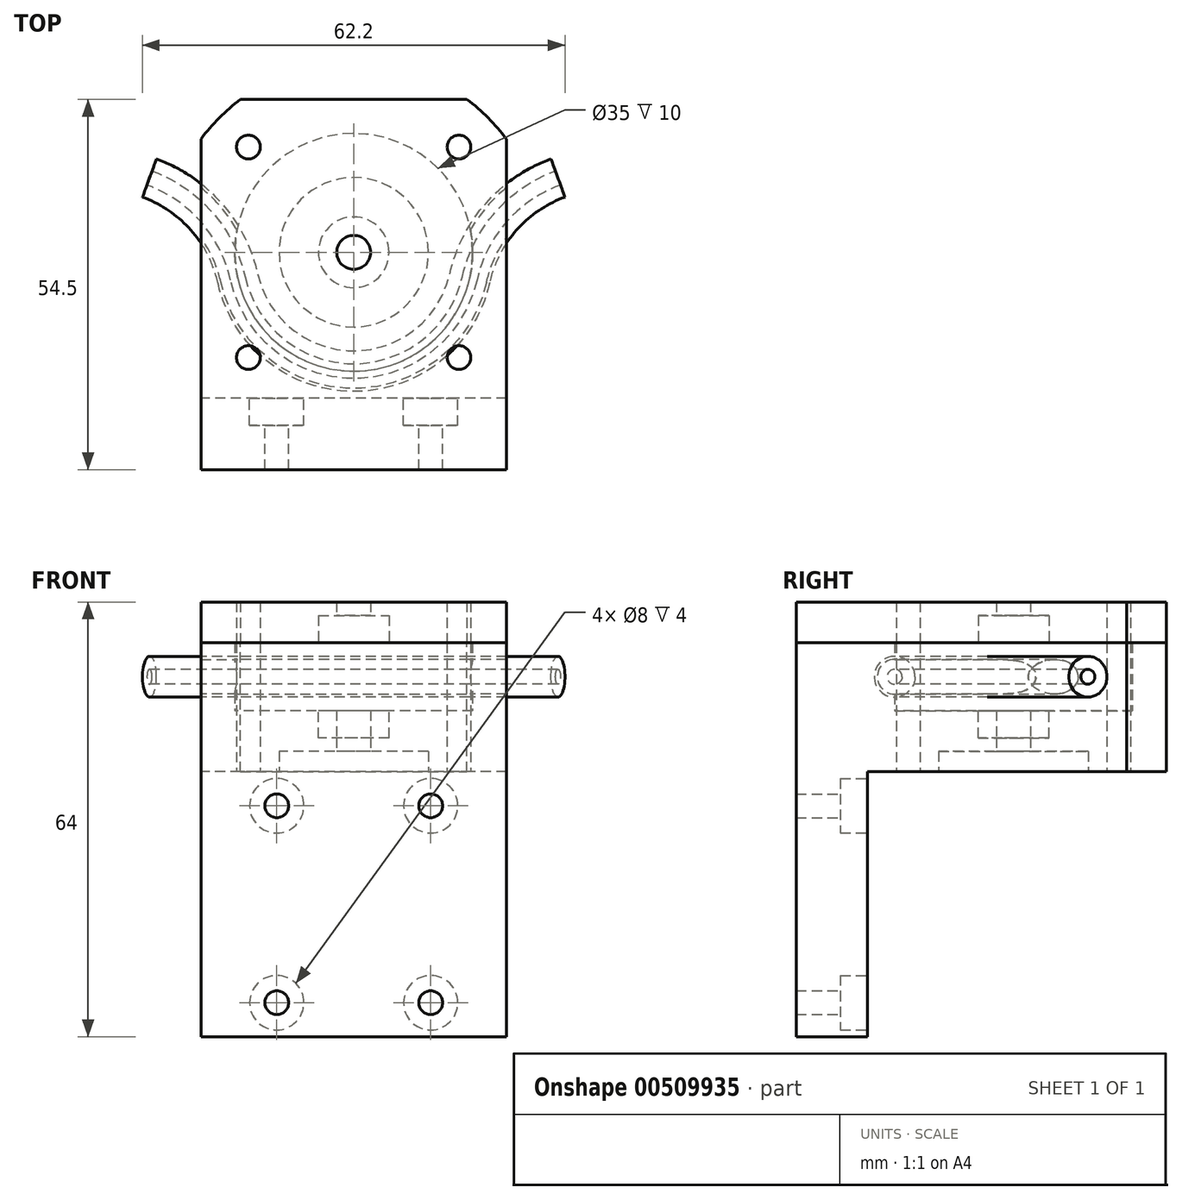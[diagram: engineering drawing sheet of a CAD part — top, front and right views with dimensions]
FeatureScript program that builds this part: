
annotation { "Feature Type Name" : "Feature", "Feature Type Description" : "" }
export const myFeature = defineFeature(function(context is Context, id is Id, definition is map)
    precondition{}
    {
        {
            var Q0;
            Q0=qCreatedBy(makeId("Top.planeOp"),FACE);
            var sketch = newSketch(context, id + "F0", { "sketchPlane" : qUnion([Q0])});
            skLineSegment(sketch, "E0", {"start": v(-21.5, -16.33) * mm, "end": v(-21.5, 16.33) * mm});
            skLineSegment(sketch, "E1", {"start": v(-16.33, 21.5) * mm, "end": v(16.33, 21.5) * mm});
            skLineSegment(sketch, "E2", {"start": v(21.5, 16.33) * mm, "end": v(21.5, -16.33) * mm});
            skLineSegment(sketch, "E3", {"start": v(16.33, -21.5) * mm, "end": v(-16.33, -21.5) * mm});
            skArc(sketch, "E4", {"start": v(-16.33, 21.5) * mm, "mid": v(-19.1, 19.1) * mm, "end": v(-21.5, 16.33) * mm});
            skArc(sketch, "E5", {"start": v(21.5, 16.33) * mm, "mid": v(19.1, 19.1) * mm, "end": v(16.33, 21.5) * mm});
            skCircle(sketch, "E6", {"center": v(-15.5, 15.5) * mm, "radius": 1.75 * mm});
            skCircle(sketch, "E7", {"center": v(15.5, 15.5) * mm, "radius": 1.75 * mm});
            skCircle(sketch, "E8", {"center": v(0, 0) * mm, "radius": 11 * mm});
            skCircle(sketch, "E9", {"center": v(-15.5, -15.5) * mm, "radius": 1.75 * mm});
            skCircle(sketch, "E10", {"center": v(15.5, -15.5) * mm, "radius": 1.75 * mm});
            skArc(sketch, "E11", {"start": v(-21.5, -16.33) * mm, "mid": v(-19.1, -19.1) * mm, "end": v(-16.33, -21.5) * mm});
            skArc(sketch, "E12", {"start": v(16.33, -21.5) * mm, "mid": v(19.1, -19.1) * mm, "end": v(21.5, -16.33) * mm});
            skLineSegment(sketch, "E13.bottom", {"start": v(15.5, 15.5) * mm, "end": v(-15.5, 15.5) * mm, "construction": true});
            skLineSegment(sketch, "E13.top", {"start": v(15.5, -15.5) * mm, "end": v(-15.5, -15.5) * mm, "construction": true});
            skLineSegment(sketch, "E13.left", {"start": v(15.5, 15.5) * mm, "end": v(15.5, -15.5) * mm, "construction": true});
            skLineSegment(sketch, "E13.right", {"start": v(-15.5, 15.5) * mm, "end": v(-15.5, -15.5) * mm, "construction": true});
            skLineSegment(sketch, "E14", {"start": v(0, 21.5) * mm, "end": v(0, -21.5) * mm, "construction": true});
            skLineSegment(sketch, "E15", {"start": v(-21.5, 0) * mm, "end": v(21.5, 0) * mm, "construction": true});
            skPoint(sketch, "E15.endSnap0", {"position": v(21.5, 0) * mm});
            skCircle(sketch, "E16", {"center": v(0, 0) * mm, "radius": 2.5 * mm});
            skSolve(sketch);
        }
        {
            var Q0;
            Q0=makeQuery(id+"F0.imprint","IMPRINT",FACE,{"disambiguationData":[TD([[makeQuery(id+"F0.imprint","IMPRINT",EDGE,{"derivedFrom":sQuery(id+"F0.wireOp",EDGE,"E0")}),-1.0]])]});
            var Q1;
            Q1=makeQuery(id+"F0.imprint","IMPRINT",FACE,{"disambiguationData":[TD([[makeQuery(id+"F0.imprint","IMPRINT",EDGE,{"derivedFrom":sQuery(id+"F0.wireOp",EDGE,"E8")}),1.0]])]});
            extrude(context, id + "F1", {"entities" : qUnion([Q0, Q1]), "depth" : 2 * mm, "offsetDistance" : 25 * mm});
        }
        {
            var Q0;
            Q0=makeQuery(id+"F1.opExtrude","CAP_FACE",FACE,{"disambiguationData":[OSD([sQuery(id+"F0.wireOp",EDGE,"E0"),sQuery(id+"F0.wireOp",EDGE,"E1"),sQuery(id+"F0.wireOp",EDGE,"E2"),sQuery(id+"F0.wireOp",EDGE,"E3"),sQuery(id+"F0.wireOp",EDGE,"E4"),sQuery(id+"F0.wireOp",EDGE,"E5"),sQuery(id+"F0.wireOp",EDGE,"E6"),sQuery(id+"F0.wireOp",EDGE,"E7"),sQuery(id+"F0.wireOp",EDGE,"E8"),sQuery(id+"F0.wireOp",EDGE,"E9"),sQuery(id+"F0.wireOp",EDGE,"E10"),sQuery(id+"F0.wireOp",EDGE,"E11"),sQuery(id+"F0.wireOp",EDGE,"E12")])],"isStart":false});
            var Q1;
            Q1=makeQuery(id+"F0.imprint","IMPRINT",FACE,{"disambiguationData":[TD([[makeQuery(id+"F0.imprint","IMPRINT",EDGE,{"derivedFrom":sQuery(id+"F0.wireOp",EDGE,"d85fea0c-31e0-45f3-b9b2-28f0fcc0159b")}),-1.0]])]});
            extrude(context, id + "F2", {"entities" : qUnion([Q0, Q1]), "operationType" : NewBodyOperationType.ADD, "depth" : 7 * mm, "offsetDistance" : 25 * mm});
        }
        {
            var Q0;
            Q0=makeQuery(id+"F2.opExtrude","CAP_FACE",FACE,{"disambiguationData":[OSD([sQuery(id+"F0.wireOp",EDGE,"E0"),sQuery(id+"F0.wireOp",EDGE,"E1"),sQuery(id+"F0.wireOp",EDGE,"E2"),sQuery(id+"F0.wireOp",EDGE,"E3"),sQuery(id+"F0.wireOp",EDGE,"E4"),sQuery(id+"F0.wireOp",EDGE,"E5"),sQuery(id+"F0.wireOp",EDGE,"E6"),sQuery(id+"F0.wireOp",EDGE,"E7"),sQuery(id+"F0.wireOp",EDGE,"E8"),sQuery(id+"F0.wireOp",EDGE,"E9"),sQuery(id+"F0.wireOp",EDGE,"E10"),sQuery(id+"F0.wireOp",EDGE,"E11"),sQuery(id+"F0.wireOp",EDGE,"E12")])],"isStart":false});
            var sketch = newSketch(context, id + "F3", { "sketchPlane" : qUnion([Q0])});
            skArc(sketch, "E17.0", {"start": v(-16.67, 22.5) * mm, "mid": v(-19.8, 19.8) * mm, "end": v(-22.5, 16.67) * mm});
            skLineSegment(sketch, "E17.1", {"start": v(-22.5, -16.67) * mm, "end": v(-22.5, 16.67) * mm});
            skLineSegment(sketch, "E17.2", {"start": v(-16.67, 22.5) * mm, "end": v(16.67, 22.5) * mm});
            skArc(sketch, "E17.3", {"start": v(-22.5, -16.67) * mm, "mid": v(-19.8, -19.8) * mm, "end": v(-16.67, -22.5) * mm});
            skArc(sketch, "E17.4", {"start": v(22.5, 16.67) * mm, "mid": v(19.8, 19.8) * mm, "end": v(16.67, 22.5) * mm});
            skLineSegment(sketch, "E17.5", {"start": v(22.5, 16.67) * mm, "end": v(22.5, -16.67) * mm});
            skArc(sketch, "E17.6", {"start": v(16.67, -22.5) * mm, "mid": v(19.8, -19.8) * mm, "end": v(22.5, -16.67) * mm});
            skLineSegment(sketch, "E17.7", {"start": v(16.67, -22.5) * mm, "end": v(-16.67, -22.5) * mm});
            skSolve(sketch);
        }
        {
            var Q0;
            Q0=makeQuery(id+"F3.imprint","IMPRINT",FACE,{"disambiguationData":[TD([[makeQuery(id+"F3.imprint","IMPRINT",EDGE,{"derivedFrom":sQuery(id+"F3.wireOp",EDGE,"E17.0")}),1.0]])]});
            extrude(context, id + "F4", {"entities" : qUnion([Q0]), "operationType" : NewBodyOperationType.ADD, "oppositeDirection" : true, "depth" : 48 * mm, "offsetDistance" : 25 * mm});
        }
        {
            var Q0;
            {var subQ0=sQuery(id+"F0.wireOp",EDGE,"E12");var subQ1=sQuery(id+"F0.wireOp",EDGE,"E11");var subQ2=sQuery(id+"F0.wireOp",EDGE,"E5");var subQ3=sQuery(id+"F0.wireOp",EDGE,"E4");var subQ4=sQuery(id+"F0.wireOp",EDGE,"E3");var subQ5=sQuery(id+"F0.wireOp",EDGE,"E2");var subQ6=sQuery(id+"F0.wireOp",EDGE,"E1");var subQ7=sQuery(id+"F0.wireOp",EDGE,"E0");Q0=makeQuery(id+"F4.boolean.opBoolean","MERGE",FACE,{"derivedFrom":[makeQuery(id+"F2.opExtrude","CAP_FACE",FACE,{"disambiguationData":[OSD([subQ7,subQ6,subQ5,subQ4,subQ3,subQ2,sQuery(id+"F0.wireOp",EDGE,"E6"),sQuery(id+"F0.wireOp",EDGE,"E7"),sQuery(id+"F0.wireOp",EDGE,"E8"),sQuery(id+"F0.wireOp",EDGE,"E9"),sQuery(id+"F0.wireOp",EDGE,"E10"),subQ1,subQ0])],"isStart":false}),makeQuery(id+"F4.opExtrude","CAP_FACE",FACE,{"disambiguationData":[OSD([subQ7,subQ6,subQ5,subQ4,subQ3,subQ2,subQ1,subQ0,sQuery(id+"F3.wireOp",EDGE,"E17.0"),sQuery(id+"F3.wireOp",EDGE,"E17.1"),sQuery(id+"F3.wireOp",EDGE,"E17.2"),sQuery(id+"F3.wireOp",EDGE,"E17.3"),sQuery(id+"F3.wireOp",EDGE,"E17.4"),sQuery(id+"F3.wireOp",EDGE,"E17.5"),sQuery(id+"F3.wireOp",EDGE,"E17.6"),sQuery(id+"F3.wireOp",EDGE,"E17.7")])],"isStart":true})]});}
            var sketch = newSketch(context, id + "F5", { "sketchPlane" : qUnion([Q0])});
            skCircle(sketch, "E18", {"center": v(0, 0) * mm, "radius": 32 * mm});
            skLineSegment(sketch, "E19", {"start": v(-22.5, -16.67) * mm, "end": v(-22.5, -32) * mm});
            skLineSegment(sketch, "E20", {"start": v(-22.5, -32) * mm, "end": v(22.5, -32) * mm});
            skLineSegment(sketch, "E21", {"start": v(22.5, -32) * mm, "end": v(22.5, -16.67) * mm});
            skCircle(sketch, "E22", {"center": v(0, 0) * mm, "radius": 17.5 * mm});
            skCircle(sketch, "E23", {"center": v(0, 0) * mm, "radius": 2.5 * mm});
            skSolve(sketch);
        }
        {
            var Q0;
            {var subQ1=sQuery(id+"F5.wireOp",EDGE,"E21");Q0=makeQuery(id+"F5.imprint","IMPRINT",FACE,{"disambiguationData":[TD([[makeQuery(id+"F5.imprint","IMPRINT",EDGE,{"derivedFrom":subQ1}),1.0]])]});}
            var Q1;
            {var subQ1=sQuery(id+"F5.wireOp",EDGE,"E19");Q1=makeQuery(id+"F5.imprint","IMPRINT",FACE,{"disambiguationData":[TD([[makeQuery(id+"F5.imprint","IMPRINT",EDGE,{"derivedFrom":subQ1}),1.0]])]});}
            var Q2;
            {var subQ0=sQuery(id+"F5.wireOp",EDGE,"E18");var subQ1=makeQuery(id+"F5.imprint","INTERSECT",VERTEX,{"derivedFrom":[subQ0,sQuery(id+"F5.wireOp",EDGE,"E20")]});Q2=makeQuery(id+"F5.imprint","IMPRINT",FACE,{"disambiguationData":[TD([[makeQuery(id+"F5.imprint","IMPRINT",EDGE,{"disambiguationData":[TD([[subQ1,1.0]])],"derivedFrom":subQ0}),1.0]])]});}
            extrude(context, id + "F6", {"entities" : qUnion([Q0, Q1, Q2]), "operationType" : NewBodyOperationType.ADD, "oppositeDirection" : true, "depth" : 48 * mm, "offsetDistance" : 25 * mm});
        }
        {
            var Q0;
            {var subQ4=sQuery(id+"F5.wireOp",EDGE,"E18");var subQ28=makeQuery(id+"F4.opExtrude","CAP_EDGE",EDGE,{"disambiguationData":[OSD([sQuery(id+"F3.wireOp",EDGE,"646ab015-f94a-48a6-a4ab-2b46942ccab2.2")])],"isStart":true});var subQ29=makeQuery(id+"F5.imprint","INTERSECT",VERTEX,{"derivedFrom":[subQ28,subQ4]});Q0=makeQuery(id+"F5.imprint","IMPRINT",FACE,{"disambiguationData":[TD([[makeQuery(id+"F5.imprint","IMPRINT",EDGE,{"disambiguationData":[TD([[subQ29,-1.0]])],"derivedFrom":subQ4}),1.0]])]});}
            var Q1;
            {var subQ0=sQuery(id+"F5.wireOp",EDGE,"E18");var subQ1=makeQuery(id+"F4.boolean.opBoolean","MERGE",EDGE,{"derivedFrom":[makeQuery(id+"F2.opExtrude","CAP_EDGE",EDGE,{"disambiguationData":[OSD([sQuery(id+"F1Hpu5VrwMmlooL_1.wireOp",EDGE,"8e26481d-0692-495c-8b6e-13f98c5af57d")])],"isStart":false}),makeQuery(id+"F4.opExtrude","CAP_EDGE",EDGE,{"disambiguationData":[OSD([sQuery(id+"F3.wireOp",EDGE,"JSha1XCR-3J3x-jMRG-RlZc-dtnEwsOd18PA")])],"isStart":true}),makeQuery(id+"F4.opExtrude","CAP_EDGE",EDGE,{"disambiguationData":[OSD([sQuery(id+"F3.wireOp",EDGE,"9211a1b2-c39d-4ab5-b8c2-9bb960df69d4.trimOffspring")])],"isStart":true})]});var subQ2=makeQuery(id+"F5.imprint","INTERSECT",VERTEX,{"disambiguationData":[OD(0.0)],"derivedFrom":[subQ1,subQ0]});Q1=makeQuery(id+"F5.imprint","IMPRINT",FACE,{"disambiguationData":[TD([[makeQuery(id+"F5.imprint","IMPRINT",EDGE,{"disambiguationData":[TD([[subQ2,-1.0]])],"derivedFrom":subQ0}),1.0]])]});}
            var Q2;
            {var subQ0=sQuery(id+"F5.wireOp",EDGE,"E18");var subQ1=makeQuery(id+"F4.opExtrude","CAP_EDGE",EDGE,{"disambiguationData":[OSD([sQuery(id+"F3.wireOp",EDGE,"646ab015-f94a-48a6-a4ab-2b46942ccab2.4")])],"isStart":true});var subQ2=makeQuery(id+"F5.imprint","INTERSECT",VERTEX,{"derivedFrom":[subQ1,subQ0]});Q2=makeQuery(id+"F5.imprint","IMPRINT",FACE,{"disambiguationData":[TD([[makeQuery(id+"F5.imprint","IMPRINT",EDGE,{"disambiguationData":[TD([[subQ2,-1.0]])],"derivedFrom":subQ0}),1.0]])]});}
            var Q3;
            {var subQ6=sQuery(id+"F5.wireOp",EDGE,"E19");Q3=makeQuery(id+"F5.imprint","IMPRINT",FACE,{"disambiguationData":[TD([[makeQuery(id+"F5.imprint","IMPRINT",EDGE,{"derivedFrom":subQ6}),1.0]])]});}
            var Q4;
            {var subQ0=sQuery(id+"F5.wireOp",EDGE,"E18");var subQ1=makeQuery(id+"F5.imprint","INTERSECT",VERTEX,{"derivedFrom":[subQ0,sQuery(id+"F5.wireOp",EDGE,"E20")]});Q4=makeQuery(id+"F5.imprint","IMPRINT",FACE,{"disambiguationData":[TD([[makeQuery(id+"F5.imprint","IMPRINT",EDGE,{"disambiguationData":[TD([[subQ1,1.0]])],"derivedFrom":subQ0}),1.0]])]});}
            var Q5;
            {var subQ6=sQuery(id+"F5.wireOp",EDGE,"E21");Q5=makeQuery(id+"F5.imprint","IMPRINT",FACE,{"disambiguationData":[TD([[makeQuery(id+"F5.imprint","IMPRINT",EDGE,{"derivedFrom":subQ6}),1.0]])]});}
            var Q6;
            {var subQ0=sQuery(id+"F5.wireOp",EDGE,"E18");var subQ1=makeQuery(id+"F4.opExtrude","CAP_EDGE",EDGE,{"disambiguationData":[OSD([sQuery(id+"F3.wireOp",EDGE,"646ab015-f94a-48a6-a4ab-2b46942ccab2.7")])],"isStart":true});var subQ2=makeQuery(id+"F5.imprint","INTERSECT",VERTEX,{"disambiguationData":[OD(0.0)],"derivedFrom":[subQ1,subQ0]});Q6=makeQuery(id+"F5.imprint","IMPRINT",FACE,{"disambiguationData":[TD([[makeQuery(id+"F5.imprint","IMPRINT",EDGE,{"disambiguationData":[TD([[subQ2,1.0]])],"derivedFrom":subQ0}),1.0]])]});}
            var Q7;
            {var subQ0=sQuery(id+"F5.wireOp",EDGE,"E22");var subQ1=makeQuery(id+"F2.opExtrude","CAP_EDGE",EDGE,{"disambiguationData":[OSD([sQuery(id+"F1Hpu5VrwMmlooL_1.wireOp",EDGE,"9a130dde-bc44-4270-aeb8-7f362e7485a4")])],"isStart":false});var subQ2=makeQuery(id+"F5.imprint","INTERSECT",VERTEX,{"disambiguationData":[OD(0.0)],"derivedFrom":[subQ1,subQ0]});Q7=makeQuery(id+"F5.imprint","IMPRINT",FACE,{"disambiguationData":[TD([[makeQuery(id+"F5.imprint","IMPRINT",EDGE,{"disambiguationData":[TD([[subQ2,-1.0]])],"derivedFrom":subQ0}),-1.0]])]});}
            var Q8;
            {var subQ0=sQuery(id+"F5.wireOp",EDGE,"E22");var subQ1=makeQuery(id+"F2.opExtrude","CAP_EDGE",EDGE,{"disambiguationData":[OSD([sQuery(id+"F1Hpu5VrwMmlooL_1.wireOp",EDGE,"1fc29757-d1f2-4ccb-9a81-5a1ceaa807c7")])],"isStart":false});var subQ2=makeQuery(id+"F5.imprint","INTERSECT",VERTEX,{"disambiguationData":[OD(0.0)],"derivedFrom":[subQ1,subQ0]});Q8=makeQuery(id+"F5.imprint","IMPRINT",FACE,{"disambiguationData":[TD([[makeQuery(id+"F5.imprint","IMPRINT",EDGE,{"disambiguationData":[TD([[subQ2,-1.0]])],"derivedFrom":subQ0}),-1.0]])]});}
            var Q9;
            {var subQ0=sQuery(id+"F5.wireOp",EDGE,"E22");var subQ1=makeQuery(id+"F2.opExtrude","CAP_EDGE",EDGE,{"disambiguationData":[OSD([sQuery(id+"F1Hpu5VrwMmlooL_1.wireOp",EDGE,"4d534888-ec9c-4465-8bad-2fd676ba325a")])],"isStart":false});var subQ2=makeQuery(id+"F5.imprint","INTERSECT",VERTEX,{"disambiguationData":[OD(0.0)],"derivedFrom":[subQ1,subQ0]});Q9=makeQuery(id+"F5.imprint","IMPRINT",FACE,{"disambiguationData":[TD([[makeQuery(id+"F5.imprint","IMPRINT",EDGE,{"disambiguationData":[TD([[subQ2,1.0]])],"derivedFrom":subQ0}),-1.0]])]});}
            var Q10;
            {var subQ0=sQuery(id+"F5.wireOp",EDGE,"E22");var subQ1=makeQuery(id+"F2.opExtrude","CAP_EDGE",EDGE,{"disambiguationData":[OSD([sQuery(id+"F1Hpu5VrwMmlooL_1.wireOp",EDGE,"5fe68f5a-298d-45ce-920e-f32339d6a1d9")])],"isStart":false});var subQ2=makeQuery(id+"F5.imprint","INTERSECT",VERTEX,{"disambiguationData":[OD(0.0)],"derivedFrom":[subQ1,subQ0]});Q10=makeQuery(id+"F5.imprint","IMPRINT",FACE,{"disambiguationData":[TD([[makeQuery(id+"F5.imprint","IMPRINT",EDGE,{"disambiguationData":[TD([[subQ2,-1.0]])],"derivedFrom":subQ0}),-1.0]])]});}
            var Q11;
            Q11=makeQuery(id+"F5.imprint","IMPRINT",FACE,{"disambiguationData":[TD([[makeQuery(id+"F5.imprint","IMPRINT",EDGE,{"derivedFrom":sQuery(id+"F5.wireOp",EDGE,"E22")}),-1.0]])]});
            extrude(context, id + "F7", {"entities" : qUnion([Q0, Q1, Q2, Q3, Q4, Q5, Q6, Q7, Q8, Q9, Q10, Q11]), "operationType" : NewBodyOperationType.ADD, "depth" : 10 * mm, "offsetDistance" : 25 * mm});
        }
        {
            var Q0;
            {var subQ4=sQuery(id+"F5.wireOp",EDGE,"E18");var subQ28=makeQuery(id+"F4.opExtrude","CAP_EDGE",EDGE,{"disambiguationData":[OSD([sQuery(id+"F3.wireOp",EDGE,"646ab015-f94a-48a6-a4ab-2b46942ccab2.2")])],"isStart":true});var subQ29=makeQuery(id+"F5.imprint","INTERSECT",VERTEX,{"derivedFrom":[subQ28,subQ4]});Q0=makeQuery(id+"F5.imprint","IMPRINT",FACE,{"disambiguationData":[TD([[makeQuery(id+"F5.imprint","IMPRINT",EDGE,{"disambiguationData":[TD([[subQ29,-1.0]])],"derivedFrom":subQ4}),1.0]])]});}
            cPlane(context, id + "F8", {"entities" : qUnion([Q0]), "cplaneType" : CPlaneType.OFFSET, "offset" : 5 * mm, "width" : 150 * mm, "height" : 150 * mm});
        }
        {
            var Q0;
            Q0=qCreatedBy(id+"F8.planeOp",FACE);
            var sketch = newSketch(context, id + "F9", { "sketchPlane" : qUnion([Q0])});
            skArc(sketch, "E24", {"start": v(-17.07, -3.83) * mm, "mid": v(0, -17.5) * mm, "end": v(17.07, -3.83) * mm});
            skArc(sketch, "E25", {"start": v(-17.07, -3.83) * mm, "mid": v(-21.68, 5.22) * mm, "end": v(-30.07, 10.94) * mm});
            skArc(sketch, "E26", {"start": v(30.07, 10.94) * mm, "mid": v(21.68, 5.22) * mm, "end": v(17.07, -3.83) * mm});
            skLineSegment(sketch, "E27", {"start": v(0, 0) * mm, "end": v(30.07, 10.94) * mm, "construction": true});
            skLineSegment(sketch, "E28", {"start": v(0, 0) * mm, "end": v(-30.07, 10.94) * mm, "construction": true});
            skLineSegment(sketch, "E29", {"start": v(-34.05, 0) * mm, "end": v(34.05, 0) * mm, "construction": true});
            skLineSegment(sketch, "E30", {"start": v(-30.07, 10.94) * mm, "end": v(-34.05, 0) * mm, "construction": true});
            skLineSegment(sketch, "E31", {"start": v(30.07, 10.94) * mm, "end": v(34.05, 0) * mm, "construction": true});
            skSolve(sketch);
        }
        {
            var Q0;
            Q0=sQuery(id+"F9.wireOp",EDGE,"E30");
            cPlane(context, id + "F10", {"entities" : qUnion([Q0]), "cplaneType" : CPlaneType.LINE_ANGLE, "offset" : 0 * mm, "angle" : 90 * degree, "width" : 150 * mm, "height" : 150 * mm});
        }
        {
            var Q0;
            Q0=qCreatedBy(id+"F10.planeOp",FACE);
            var sketch = newSketch(context, id + "F11", { "sketchPlane" : qUnion([Q0])});
            skCircle(sketch, "E32", {"center": v(0, 14) * mm, "radius": 3 * mm});
            skCircle(sketch, "E33", {"center": v(0, 14) * mm, "radius": 1.1 * mm});
            skSolve(sketch);
        }
        {
            var Q0;
            Q0=sQuery(id+"F9.wireOp",EDGE,"E31");
            cPlane(context, id + "F12", {"entities" : qUnion([Q0]), "cplaneType" : CPlaneType.LINE_ANGLE, "offset" : 2.5 * mm, "angle" : 90 * degree, "width" : 150 * mm, "height" : 150 * mm});
        }
        {
            var Q0;
            Q0=qCreatedBy(id+"F12.planeOp",FACE);
            var sketch = newSketch(context, id + "F13", { "sketchPlane" : qUnion([Q0])});
            skCircle(sketch, "E34", {"center": v(0, 14) * mm, "radius": 2.55 * mm});
            skSolve(sketch);
        }
        {
            var Q0;
            Q0=makeQuery(id+"F13.imprint","IMPRINT",FACE,{"disambiguationData":[TD([[makeQuery(id+"F13.imprint","IMPRINT",EDGE,{"derivedFrom":sQuery(id+"F13.wireOp",EDGE,"E34")}),1.0]])]});
            var Q1;
            Q1 = qConstructionFilter(qBodyType(qCreatedBy(id + "F9" ,EDGE), BodyType.WIRE), ConstructionObject.NO);
            sweep(context, id + "F14", {"operationType" : NewBodyOperationType.REMOVE, "profiles" : qUnion([Q0]), "path" : qUnion([Q1])});
        }
        {
            var Q0;
            Q0=makeQuery(id+"F7.opExtrude","CAP_FACE",FACE,{"disambiguationData":[OSD([sQuery(id+"F3.wireOp",EDGE,"646ab015-f94a-48a6-a4ab-2b46942ccab2.0"),sQuery(id+"F3.wireOp",EDGE,"646ab015-f94a-48a6-a4ab-2b46942ccab2.1"),sQuery(id+"F3.wireOp",EDGE,"646ab015-f94a-48a6-a4ab-2b46942ccab2.3"),sQuery(id+"F5.wireOp",EDGE,"E18"),sQuery(id+"F5.wireOp",EDGE,"E19"),sQuery(id+"F5.wireOp",EDGE,"E20"),sQuery(id+"F5.wireOp",EDGE,"E21"),sQuery(id+"F5.wireOp",EDGE,"E22")])],"isStart":false});
            var sketch = newSketch(context, id + "F15", { "sketchPlane" : qUnion([Q0])});
            skCircle(sketch, "E35", {"center": v(0, 0) * mm, "radius": 31.47 * mm});
            skCircle(sketch, "E36", {"center": v(0, 0) * mm, "radius": 2.5 * mm});
            skSolve(sketch);
        }
        {
            var Q0;
            Q0=makeQuery(id+"F15.imprint","IMPRINT",FACE,{"disambiguationData":[TD([[makeQuery(id+"F15.imprint","IMPRINT",EDGE,{"derivedFrom":sQuery(id+"F15.wireOp",EDGE,"E36")}),-1.0]])]});
            var Q1;
            Q1=makeQuery(id+"F15.imprint","IMPRINT",FACE,{"disambiguationData":[TD([[makeQuery(id+"F15.imprint","IMPRINT",EDGE,{"derivedFrom":makeQuery(id+"F7.opExtrude","CAP_EDGE",EDGE,{"disambiguationData":[OSD([sQuery(id+"F5.wireOp",EDGE,"E22")])],"isStart":false})}),-1.0]])]});
            var Q2;
            {var subQ5=makeQuery(id+"F7.opExtrude","CAP_EDGE",EDGE,{"disambiguationData":[OSD([sQuery(id+"F5.wireOp",EDGE,"E20")])],"isStart":false});Q2=makeQuery(id+"F15.imprint","IMPRINT",FACE,{"disambiguationData":[TD([[makeQuery(id+"F15.imprint","IMPRINT",EDGE,{"derivedFrom":subQ5}),1.0]])]});}
            var Q3;
            {var subQ1=sQuery(id+"F3.wireOp",EDGE,"E17.2");var subQ7=sQuery(id+"F5.wireOp",EDGE,"E18");var subQ8=makeQuery(id+"F7.opExtrude","CAP_EDGE",EDGE,{"disambiguationData":[OSD([subQ7]),TDD([makeQuery(id+"F5.imprint","IMPRINT",EDGE,{"disambiguationData":[TD([[makeQuery(id+"F5.imprint","INTERSECT",VERTEX,{"disambiguationData":[OD(1.0)],"derivedFrom":[makeQuery(id+"F4.opExtrude","CAP_EDGE",EDGE,{"disambiguationData":[OSD([subQ1])],"isStart":true}),subQ7]}),1.0]])],"derivedFrom":subQ7})])],"isStart":false});Q3=makeQuery(id+"F15.imprint","IMPRINT",FACE,{"disambiguationData":[TD([[makeQuery(id+"F15.imprint","IMPRINT",EDGE,{"derivedFrom":subQ8}),1.0]])]});}
            var Q4;
            {var subQ1=sQuery(id+"F3.wireOp",EDGE,"E17.2");var subQ7=sQuery(id+"F5.wireOp",EDGE,"E18");var subQ8=makeQuery(id+"F7.opExtrude","CAP_EDGE",EDGE,{"disambiguationData":[OSD([subQ7]),TDD([makeQuery(id+"F5.imprint","IMPRINT",EDGE,{"disambiguationData":[TD([[makeQuery(id+"F5.imprint","INTERSECT",VERTEX,{"disambiguationData":[OD(0.0)],"derivedFrom":[makeQuery(id+"F4.opExtrude","CAP_EDGE",EDGE,{"disambiguationData":[OSD([subQ1])],"isStart":true}),subQ7]}),-1.0]])],"derivedFrom":subQ7})])],"isStart":false});Q4=makeQuery(id+"F15.imprint","IMPRINT",FACE,{"disambiguationData":[TD([[makeQuery(id+"F15.imprint","IMPRINT",EDGE,{"derivedFrom":subQ8}),1.0]])]});}
            extrude(context, id + "F16", {"entities" : qUnion([Q0, Q1, Q2, Q3, Q4]), "depth" : 6 * mm, "offsetDistance" : 25 * mm});
        }
        {
            var Q0;
            Q0=makeQuery(id+"F16.opExtrude","CAP_FACE",FACE,{"disambiguationData":[OSD([sQuery(id+"F1Hpu5VrwMmlooL_1.wireOp",EDGE,"8e26481d-0692-495c-8b6e-13f98c5af57d"),sQuery(id+"F1Hpu5VrwMmlooL_1.wireOp",EDGE,"5fe68f5a-298d-45ce-920e-f32339d6a1d9"),sQuery(id+"F1Hpu5VrwMmlooL_1.wireOp",EDGE,"4d534888-ec9c-4465-8bad-2fd676ba325a"),sQuery(id+"F1Hpu5VrwMmlooL_1.wireOp",EDGE,"9a130dde-bc44-4270-aeb8-7f362e7485a4"),sQuery(id+"F1Hpu5VrwMmlooL_1.wireOp",EDGE,"1fc29757-d1f2-4ccb-9a81-5a1ceaa807c7"),sQuery(id+"F3.wireOp",EDGE,"646ab015-f94a-48a6-a4ab-2b46942ccab2.2"),sQuery(id+"F3.wireOp",EDGE,"646ab015-f94a-48a6-a4ab-2b46942ccab2.4"),sQuery(id+"F3.wireOp",EDGE,"646ab015-f94a-48a6-a4ab-2b46942ccab2.7"),sQuery(id+"F3.wireOp",EDGE,"JSha1XCR-3J3x-jMRG-RlZc-dtnEwsOd18PA"),sQuery(id+"F3.wireOp",EDGE,"9211a1b2-c39d-4ab5-b8c2-9bb960df69d4.trimOffspring"),sQuery(id+"F5.wireOp",EDGE,"E19"),sQuery(id+"F5.wireOp",EDGE,"E20"),sQuery(id+"F5.wireOp",EDGE,"E21"),sQuery(id+"F15.wireOp",EDGE,"E35"),sQuery(id+"F15.wireOp",EDGE,"E36")])],"isStart":true});
            var sketch = newSketch(context, id + "F17", { "sketchPlane" : qUnion([Q0])});
            skCircle(sketch, "E37", {"center": v(0, 0) * mm, "radius": 5.2 * mm});
            skSolve(sketch);
        }
        {
            var Q0;
            Q0=makeQuery(id+"F17.imprint","IMPRINT",FACE,{"disambiguationData":[TD([[makeQuery(id+"F17.imprint","IMPRINT",EDGE,{"derivedFrom":sQuery(id+"F17.wireOp",EDGE,"E37")}),1.0]])]});
            extrude(context, id + "F18", {"entities" : qUnion([Q0]), "operationType" : NewBodyOperationType.REMOVE, "oppositeDirection" : true, "depth" : 4 * mm, "offsetDistance" : 25 * mm});
        }
        {
            var Q0;
            {var subQ0=sQuery(id+"F3.wireOp",EDGE,"646ab015-f94a-48a6-a4ab-2b46942ccab2.3");var subQ1=sQuery(id+"F3.wireOp",EDGE,"646ab015-f94a-48a6-a4ab-2b46942ccab2.1");var subQ2=sQuery(id+"F3.wireOp",EDGE,"646ab015-f94a-48a6-a4ab-2b46942ccab2.0");Q0=makeQuery(id+"F6.boolean.opBoolean","MERGE",FACE,{"derivedFrom":[makeQuery(id+"F4.boolean.opBoolean","MERGE",FACE,{"derivedFrom":[makeQuery(id+"F2.opExtrude","CAP_FACE",FACE,{"disambiguationData":[OSD([sQuery(id+"F1Hpu5VrwMmlooL_1.wireOp",EDGE,"bdebe98e-508b-4dc6-81ce-e9b0915b905b"),sQuery(id+"F1Hpu5VrwMmlooL_1.wireOp",EDGE,"8e26481d-0692-495c-8b6e-13f98c5af57d"),sQuery(id+"F1Hpu5VrwMmlooL_1.wireOp",EDGE,"730d604f-0751-4adf-84c4-564d4acc1bf2"),sQuery(id+"F1Hpu5VrwMmlooL_1.wireOp",EDGE,"3ae73026-240c-434e-8128-a4e5a43a5ace"),sQuery(id+"F1Hpu5VrwMmlooL_1.wireOp",EDGE,"67bd35a3-ead6-4aac-8275-85918547268a"),sQuery(id+"F1Hpu5VrwMmlooL_1.wireOp",EDGE,"ca31c680-71a9-4e06-93d3-dcdf511aacea"),sQuery(id+"F1Hpu5VrwMmlooL_1.wireOp",EDGE,"5fe68f5a-298d-45ce-920e-f32339d6a1d9"),sQuery(id+"F1Hpu5VrwMmlooL_1.wireOp",EDGE,"4d534888-ec9c-4465-8bad-2fd676ba325a"),sQuery(id+"F1Hpu5VrwMmlooL_1.wireOp",EDGE,"9a130dde-bc44-4270-aeb8-7f362e7485a4"),sQuery(id+"F1Hpu5VrwMmlooL_1.wireOp",EDGE,"1fc29757-d1f2-4ccb-9a81-5a1ceaa807c7"),sQuery(id+"F1Hpu5VrwMmlooL_1.wireOp",EDGE,"e0ca1a5b-4a5a-4701-b7b4-a9afa6e3c82b"),sQuery(id+"F1Hpu5VrwMmlooL_1.wireOp",EDGE,"f9228ba7-bf05-45cf-b3cc-3e8c137fda38"),sQuery(id+"F1Hpu5VrwMmlooL_1.wireOp",EDGE,"aa8661ea-3af5-4901-8aae-093f1f5eb203")])],"isStart":false}),makeQuery(id+"F4.opExtrude","CAP_FACE",FACE,{"disambiguationData":[OSD([sQuery(id+"F3.wireOp",EDGE,"3a0f54d8-991b-4f62-906c-7d67a353449a"),sQuery(id+"F3.wireOp",EDGE,"98a7e771-4bfb-4205-8b27-0b6975573ff0"),sQuery(id+"F3.wireOp",EDGE,"4c77cdeb-d146-4bfc-8ccc-5c3fcd001468"),sQuery(id+"F3.wireOp",EDGE,"460aea3b-1a94-4910-b809-b134830fa8c7"),sQuery(id+"F3.wireOp",EDGE,"872af010-c28f-43d9-90a7-629491c90a93"),sQuery(id+"F3.wireOp",EDGE,"7882bdaf-68c7-4416-8fdf-58388a205b18"),sQuery(id+"F3.wireOp",EDGE,"9d6daaff-0767-4eaf-b26b-b552bb5ee980"),subQ2,subQ1,sQuery(id+"F3.wireOp",EDGE,"646ab015-f94a-48a6-a4ab-2b46942ccab2.2"),subQ0,sQuery(id+"F3.wireOp",EDGE,"646ab015-f94a-48a6-a4ab-2b46942ccab2.4"),sQuery(id+"F3.wireOp",EDGE,"646ab015-f94a-48a6-a4ab-2b46942ccab2.6"),sQuery(id+"F3.wireOp",EDGE,"646ab015-f94a-48a6-a4ab-2b46942ccab2.7"),sQuery(id+"F3.wireOp",EDGE,"JSha1XCR-3J3x-jMRG-RlZc-dtnEwsOd18PA"),sQuery(id+"F3.wireOp",EDGE,"9211a1b2-c39d-4ab5-b8c2-9bb960df69d4.trimOffspring")])],"isStart":true})]}),makeQuery(id+"F6.opExtrude","CAP_FACE",FACE,{"disambiguationData":[OSD([subQ2,subQ1,subQ0,sQuery(id+"F5.wireOp",EDGE,"E19"),sQuery(id+"F5.wireOp",EDGE,"E20"),sQuery(id+"F5.wireOp",EDGE,"E21")])],"isStart":true})]});}
            var sketch = newSketch(context, id + "F19", { "sketchPlane" : qUnion([Q0])});
            skCircle(sketch, "E38", {"center": v(0, 0) * mm, "radius": 5.2 * mm});
            skSolve(sketch);
        }
        {
            var Q0;
            Q0=makeQuery(id+"F19.imprint","IMPRINT",FACE,{"disambiguationData":[TD([[makeQuery(id+"F19.imprint","IMPRINT",EDGE,{"derivedFrom":sQuery(id+"F19.wireOp",EDGE,"E38")}),1.0]])]});
            extrude(context, id + "F20", {"entities" : qUnion([Q0]), "operationType" : NewBodyOperationType.REMOVE, "oppositeDirection" : true, "depth" : 4 * mm, "offsetDistance" : 25 * mm});
        }
        {
            var Q0;
            Q0=makeQuery(id+"F20.boolean.opBoolean","COPY",FACE,{"derivedFrom":makeQuery(id+"F20.opExtrude","CAP_FACE",FACE,{"disambiguationData":[OSD([sQuery(id+"F1Hpu5VrwMmlooL_1.wireOp",EDGE,"aa8661ea-3af5-4901-8aae-093f1f5eb203"),sQuery(id+"F19.wireOp",EDGE,"E38")])],"isStart":false})});
            extrude(context, id + "F21", {"entities" : qUnion([Q0]), "depth" : 4 * mm, "offsetDistance" : 25 * mm});
        }
        {
            var Q0;
            Q0=makeQuery(id+"F4.opExtrude","SWEPT_FACE",FACE,{"disambiguationData":[OSD([sQuery(id+"F0.wireOp",EDGE,"E3")])]});
            var sketch = newSketch(context, id + "F22", { "sketchPlane" : qUnion([Q0])});
            skCircle(sketch, "E39", {"center": v(-11.33, -5) * mm, "radius": 1.75 * mm});
            skCircle(sketch, "E40", {"center": v(-11.33, -34) * mm, "radius": 1.75 * mm});
            skCircle(sketch, "E41", {"center": v(11.33, -34) * mm, "radius": 1.75 * mm});
            skCircle(sketch, "E42", {"center": v(11.33, -5) * mm, "radius": 1.75 * mm});
            skCircle(sketch, "E43", {"center": v(-11.33, -34) * mm, "radius": 4 * mm});
            skCircle(sketch, "E44", {"center": v(-11.33, -5) * mm, "radius": 4 * mm});
            skCircle(sketch, "E45", {"center": v(11.33, -5) * mm, "radius": 4 * mm});
            skCircle(sketch, "E46", {"center": v(11.33, -34) * mm, "radius": 4 * mm});
            skLineSegment(sketch, "E47.bottom", {"start": v(11.33, -34) * mm, "end": v(-11.33, -34) * mm, "construction": true});
            skLineSegment(sketch, "E47.top", {"start": v(11.33, -5) * mm, "end": v(-11.33, -5) * mm, "construction": true});
            skLineSegment(sketch, "E47.left", {"start": v(11.33, -34) * mm, "end": v(11.33, -5) * mm, "construction": true});
            skLineSegment(sketch, "E47.right", {"start": v(-11.33, -34) * mm, "end": v(-11.33, -5) * mm, "construction": true});
            skPoint(sketch, "E47.middle", {"position": v(0, -19.5) * mm});
            skPoint(sketch, "E47.middle.positionSnap0", {"position": v(16.33, -19.5) * mm});
            skPoint(sketch, "E47.centerSnap0", {"position": v(16.33, -19.5) * mm});
            skSolve(sketch);
        }
        {
            var Q0;
            Q0=makeQuery(id+"F22.imprint","IMPRINT",FACE,{"disambiguationData":[TD([[makeQuery(id+"F22.imprint","IMPRINT",EDGE,{"derivedFrom":sQuery(id+"F22.wireOp",EDGE,"E39")}),1.0]])]});
            var Q1;
            Q1=makeQuery(id+"F22.imprint","IMPRINT",FACE,{"disambiguationData":[TD([[makeQuery(id+"F22.imprint","IMPRINT",EDGE,{"derivedFrom":sQuery(id+"F22.wireOp",EDGE,"E42")}),1.0]])]});
            var Q2;
            Q2=makeQuery(id+"F22.imprint","IMPRINT",FACE,{"disambiguationData":[TD([[makeQuery(id+"F22.imprint","IMPRINT",EDGE,{"derivedFrom":sQuery(id+"F22.wireOp",EDGE,"E41")}),1.0]])]});
            var Q3;
            Q3=makeQuery(id+"F22.imprint","IMPRINT",FACE,{"disambiguationData":[TD([[makeQuery(id+"F22.imprint","IMPRINT",EDGE,{"derivedFrom":sQuery(id+"F22.wireOp",EDGE,"E40")}),1.0]])]});
            var Q4;
            {var subQ0=sQuery(id+"F5.wireOp",EDGE,"E20");Q4=makeQuery(id+"F7.boolean.opBoolean","MERGE",FACE,{"derivedFrom":[makeQuery(id+"F6.opExtrude","SWEPT_FACE",FACE,{"disambiguationData":[OSD([subQ0])]}),makeQuery(id+"F7.opExtrude","SWEPT_FACE",FACE,{"disambiguationData":[OSD([subQ0])]})]});}
            extrude(context, id + "F23", {"entities" : qUnion([Q0, Q1, Q2, Q3]), "operationType" : NewBodyOperationType.REMOVE, "endBound" : BoundingType.UP_TO_SURFACE, "oppositeDirection" : true, "depth" : 25 * mm, "endBoundEntityFace" : qUnion([Q4]), "offsetDistance" : 25 * mm});
        }
        {
            var Q0;
            Q0=makeQuery(id+"F22.imprint","IMPRINT",FACE,{"disambiguationData":[TD([[makeQuery(id+"F22.imprint","IMPRINT",EDGE,{"derivedFrom":sQuery(id+"F22.wireOp",EDGE,"E40")}),-1.0]])]});
            var Q1;
            Q1=makeQuery(id+"F22.imprint","IMPRINT",FACE,{"disambiguationData":[TD([[makeQuery(id+"F22.imprint","IMPRINT",EDGE,{"derivedFrom":sQuery(id+"F22.wireOp",EDGE,"E41")}),-1.0]])]});
            var Q2;
            Q2=makeQuery(id+"F22.imprint","IMPRINT",FACE,{"disambiguationData":[TD([[makeQuery(id+"F22.imprint","IMPRINT",EDGE,{"derivedFrom":sQuery(id+"F22.wireOp",EDGE,"E42")}),-1.0]])]});
            var Q3;
            Q3=makeQuery(id+"F22.imprint","IMPRINT",FACE,{"disambiguationData":[TD([[makeQuery(id+"F22.imprint","IMPRINT",EDGE,{"derivedFrom":sQuery(id+"F22.wireOp",EDGE,"E39")}),-1.0]])]});
            extrude(context, id + "F24", {"entities" : qUnion([Q0, Q1, Q2, Q3]), "operationType" : NewBodyOperationType.REMOVE, "oppositeDirection" : true, "depth" : 4 * mm, "offsetDistance" : 25 * mm});
        }
        {
            var Q0;
            Q0=makeQuery(id+"F0.imprint","IMPRINT",FACE,{"disambiguationData":[TD([[makeQuery(id+"F0.imprint","IMPRINT",EDGE,{"derivedFrom":sQuery(id+"F0.wireOp",EDGE,"E8")}),1.0]])]});
            extrude(context, id + "F25", {"entities" : qUnion([Q0]), "operationType" : NewBodyOperationType.REMOVE, "depth" : 3 * mm, "offsetDistance" : 25 * mm});
        }
        {
            var Q0;
            {var subQ0=sQuery(id+"F3.wireOp",EDGE,"E17.7");var subQ1=sQuery(id+"F3.wireOp",EDGE,"E17.6");var subQ2=sQuery(id+"F3.wireOp",EDGE,"E17.3");Q0=makeQuery(id+"F6.boolean.opBoolean","MERGE",FACE,{"derivedFrom":[makeQuery(id+"F4.opExtrude","CAP_FACE",FACE,{"disambiguationData":[OSD([sQuery(id+"F0.wireOp",EDGE,"E0"),sQuery(id+"F0.wireOp",EDGE,"E1"),sQuery(id+"F0.wireOp",EDGE,"E2"),sQuery(id+"F0.wireOp",EDGE,"E3"),sQuery(id+"F0.wireOp",EDGE,"E4"),sQuery(id+"F0.wireOp",EDGE,"E5"),sQuery(id+"F0.wireOp",EDGE,"E11"),sQuery(id+"F0.wireOp",EDGE,"E12"),sQuery(id+"F3.wireOp",EDGE,"E17.0"),sQuery(id+"F3.wireOp",EDGE,"E17.1"),sQuery(id+"F3.wireOp",EDGE,"E17.2"),subQ2,sQuery(id+"F3.wireOp",EDGE,"E17.4"),sQuery(id+"F3.wireOp",EDGE,"E17.5"),subQ1,subQ0])],"isStart":false}),makeQuery(id+"F6.opExtrude","CAP_FACE",FACE,{"disambiguationData":[OSD([subQ2,subQ1,subQ0,sQuery(id+"F5.wireOp",EDGE,"E19"),sQuery(id+"F5.wireOp",EDGE,"E20"),sQuery(id+"F5.wireOp",EDGE,"E21")])],"isStart":false})]});}
            var sketch = newSketch(context, id + "F26", { "sketchPlane" : qUnion([Q0])});
            skLineSegment(sketch, "E48", {"start": v(22.5, 21.5) * mm, "end": v(-22.5, 21.5) * mm});
            skSolve(sketch);
        }
        {
            var Q0;
            {var subQ8=makeQuery(id+"F4.opExtrude","CAP_EDGE",EDGE,{"disambiguationData":[OSD([sQuery(id+"F3.wireOp",EDGE,"E17.0")])],"isStart":false});Q0=makeQuery(id+"F26.imprint","IMPRINT",FACE,{"disambiguationData":[TD([[makeQuery(id+"F26.imprint","IMPRINT",EDGE,{"derivedFrom":subQ8}),-1.0]])]});}
            var Q1;
            Q1=makeQuery(id+"F1.opExtrude","CAP_FACE",FACE,{"disambiguationData":[OSD([sQuery(id+"F0.wireOp",EDGE,"E0"),sQuery(id+"F0.wireOp",EDGE,"E1"),sQuery(id+"F0.wireOp",EDGE,"E2"),sQuery(id+"F0.wireOp",EDGE,"E3"),sQuery(id+"F0.wireOp",EDGE,"E4"),sQuery(id+"F0.wireOp",EDGE,"E5"),sQuery(id+"F0.wireOp",EDGE,"E6"),sQuery(id+"F0.wireOp",EDGE,"E7"),sQuery(id+"F0.wireOp",EDGE,"E9"),sQuery(id+"F0.wireOp",EDGE,"E10"),sQuery(id+"F0.wireOp",EDGE,"E11"),sQuery(id+"F0.wireOp",EDGE,"E12"),sQuery(id+"F0.wireOp",EDGE,"E16")])],"isStart":true});
            extrude(context, id + "F27", {"entities" : qUnion([Q0]), "operationType" : NewBodyOperationType.REMOVE, "endBound" : BoundingType.UP_TO_SURFACE, "oppositeDirection" : true, "depth" : 25 * mm, "endBoundEntityFace" : qUnion([Q1]), "offsetDistance" : 25 * mm});
        }
        {
            var Q0;
            Q0 = qSketchRegion(id + "F11", true);
            var Q1;
            Q1=sQuery(id+"F9.wireOp",EDGE,"E25");
            var Q2;
            Q2=sQuery(id+"F9.wireOp",EDGE,"E24");
            var Q3;
            Q3=sQuery(id+"F9.wireOp",EDGE,"E26");
            sweep(context, id + "F28", {"profiles" : qUnion([Q0]), "path" : qUnion([Q1, Q2, Q3])});
        }
    });
